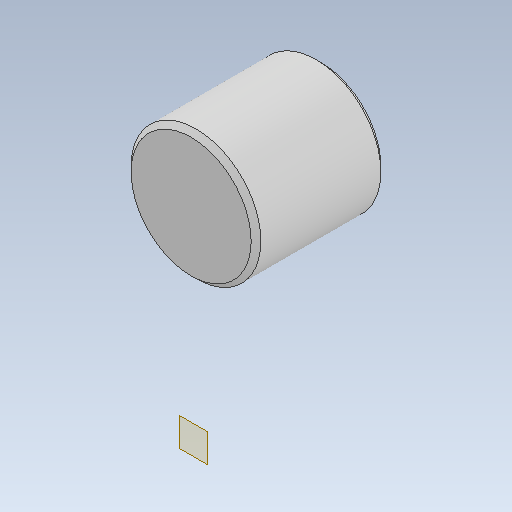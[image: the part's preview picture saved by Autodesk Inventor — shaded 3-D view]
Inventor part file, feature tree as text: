
AUTODESK INVENTOR PART (.ipt)
format: ipt  version: 2021 (Build 250183000, 183)  size: 107,008 bytes
history: native  units: mm
features: other x5, extrude x1, chamfer x1, reference x1
ambient origin geometry x8: Origin, YZ Plane, XZ Plane, XY Plane, X Axis, Y Axis, Z Axis, Center Point
bodies: Body1 (feature_tree)
feature tree (8):
  other  "Bryła1"
  other  "Płaszczyzna konstrukcyjna1"
  extrude  "Wyciągnięcie proste1"  Depth=80.0mm
  chamfer  "Faza1"  Distance=80.0mm
  reference  "Odniesienie1"
  other  "cw12model.iam"
  other  "shaft:1"
  other  "rurka:2"
